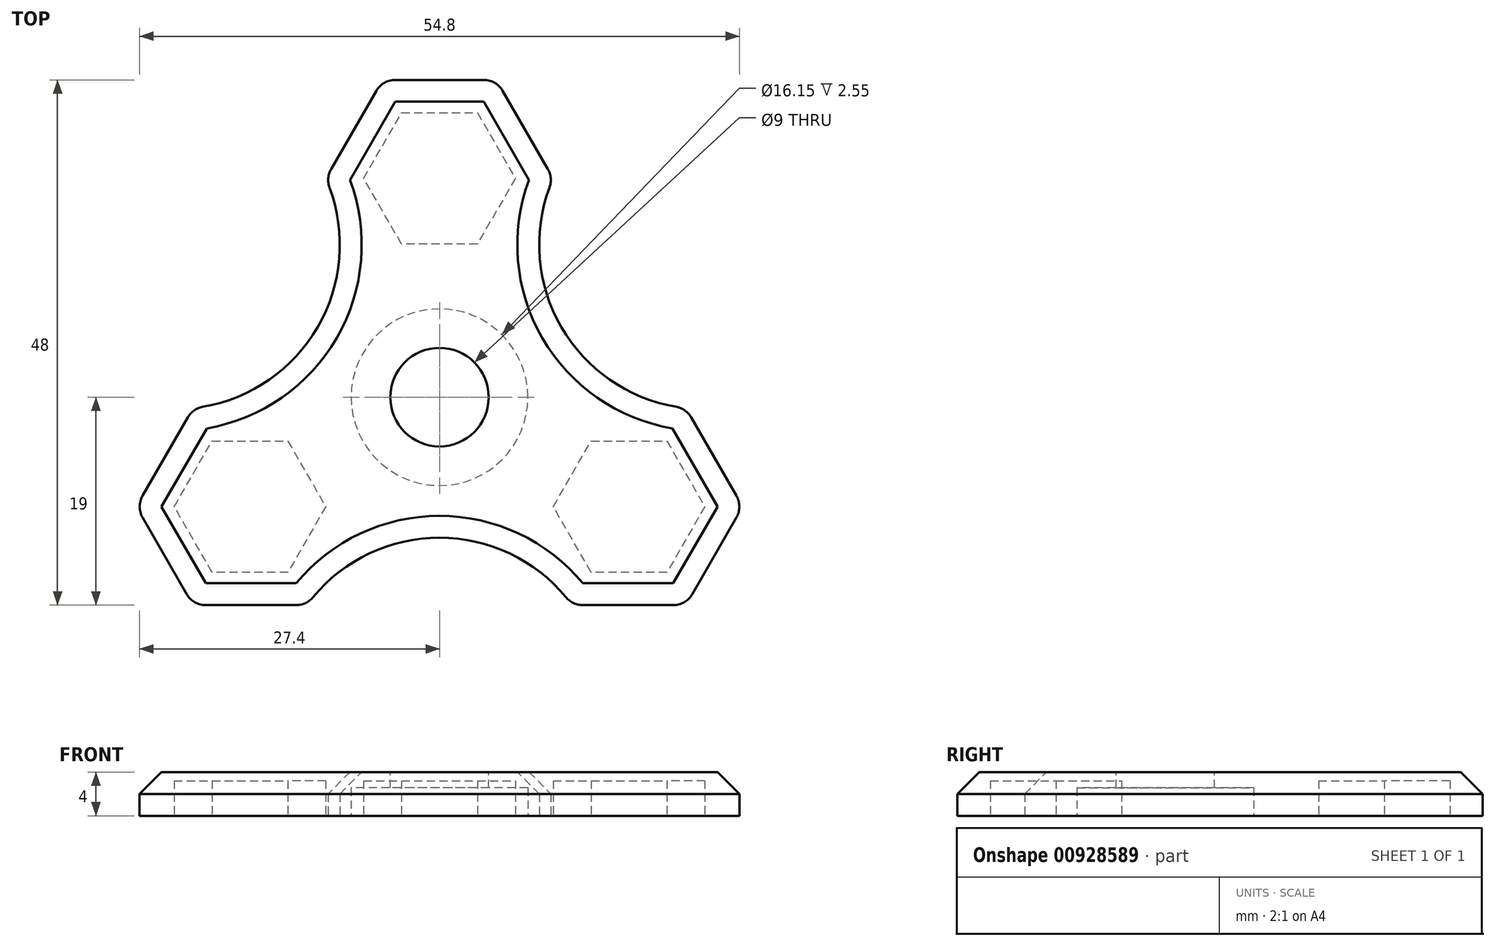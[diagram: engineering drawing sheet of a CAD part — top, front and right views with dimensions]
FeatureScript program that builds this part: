
annotation { "Feature Type Name" : "Feature", "Feature Type Description" : "" }
export const myFeature = defineFeature(function(context is Context, id is Id, definition is map)
    precondition{}
    {
        {
            var Q0;
            Q0=qCreatedBy(makeId("Top.planeOp"),FACE);
            var sketch = newSketch(context, id + "F0", { "sketchPlane" : qUnion([Q0])});
            skCircle(sketch, "E0", {"center": v(0, 0) * mm, "radius": 8 * mm, "construction": true});
            skCircle(sketch, "E1.cCircle", {"center": v(0, 20) * mm, "radius": 6 * mm, "construction": true});
            skLineSegment(sketch, "E1.0", {"start": v(3.46, 14) * mm, "end": v(-3.46, 14) * mm, "construction": true});
            skLineSegment(sketch, "E1.1", {"start": v(-3.46, 14) * mm, "end": v(-6.93, 20) * mm, "construction": true});
            skLineSegment(sketch, "E1.2", {"start": v(-6.93, 20) * mm, "end": v(-3.46, 26) * mm, "construction": true});
            skLineSegment(sketch, "E1.3", {"start": v(-3.46, 26) * mm, "end": v(3.46, 26) * mm, "construction": true});
            skLineSegment(sketch, "E1.4", {"start": v(3.46, 26) * mm, "end": v(6.93, 20) * mm, "construction": true});
            skLineSegment(sketch, "E1.5", {"start": v(6.93, 20) * mm, "end": v(3.46, 14) * mm, "construction": true});
            skPoint(sketch, "E1.0.midPoint", {"position": v(0, 14) * mm});
            skCircle(sketch, "E2.cCircle", {"center": v(0, 20) * mm, "radius": 9 * mm, "construction": true});
            skLineSegment(sketch, "E2.2", {"start": v(-9.9, 20.85) * mm, "end": v(-5.77, 28) * mm});
            skLineSegment(sketch, "E2.3", {"start": v(-4.04, 29) * mm, "end": v(4.04, 29) * mm});
            skLineSegment(sketch, "E2.4", {"start": v(5.77, 28) * mm, "end": v(9.9, 20.85) * mm});
            skPoint(sketch, "E2.0.midPoint", {"position": v(0, 11) * mm});
            skLineSegment(sketch, "E3.1.0", {"start": v(-23.1, -18) * mm, "end": v(-27.14, -11) * mm});
            skLineSegment(sketch, "E3.1.1", {"start": v(-27.14, -9) * mm, "end": v(-23, -1.85) * mm});
            skLineSegment(sketch, "E3.1.5", {"start": v(-13.1, -19) * mm, "end": v(-21.36, -19) * mm});
            skLineSegment(sketch, "E3.2.0", {"start": v(27.14, -11) * mm, "end": v(23.1, -18) * mm});
            skLineSegment(sketch, "E3.2.1", {"start": v(21.36, -19) * mm, "end": v(13.1, -19) * mm});
            skLineSegment(sketch, "E3.2.5", {"start": v(23, -1.85) * mm, "end": v(27.14, -9) * mm});
            skArc(sketch, "E4", {"start": v(10.05, 19.15) * mm, "mid": v(11.12, 6.42) * mm, "end": v(21.6, -0.87) * mm});
            skArc(sketch, "E5.1.0", {"start": v(-21.6, -0.87) * mm, "mid": v(-11.12, 6.42) * mm, "end": v(-10.05, 19.15) * mm});
            skArc(sketch, "E5.2.0", {"start": v(11.56, -18.28) * mm, "mid": v(0, -12.84) * mm, "end": v(-11.56, -18.28) * mm});
            skPoint(sketch, "E6.orphan", {"position": v(5.2, 11) * mm});
            skPoint(sketch, "E7.orphan", {"position": v(-5.2, 11) * mm});
            skPoint(sketch, "E8.visualSharp", {"position": v(-22.52, -1) * mm});
            skArc(sketch, "E8.filletArc", {"start": v(-21.6, -0.87) * mm, "mid": v(-22.42, -1.2) * mm, "end": v(-23, -1.85) * mm});
            skPoint(sketch, "E9.visualSharp", {"position": v(-27.71, -10) * mm});
            skArc(sketch, "E9.filletArc", {"start": v(-27.14, -9) * mm, "mid": v(-27.4, -10) * mm, "end": v(-27.14, -11) * mm});
            skPoint(sketch, "E10.visualSharp", {"position": v(-22.52, -19) * mm});
            skArc(sketch, "E10.filletArc", {"start": v(-23.1, -18) * mm, "mid": v(-22.36, -18.73) * mm, "end": v(-21.36, -19) * mm});
            skPoint(sketch, "E11.visualSharp", {"position": v(-12.12, -19) * mm});
            skArc(sketch, "E11.filletArc", {"start": v(-13.1, -19) * mm, "mid": v(-12.25, -18.81) * mm, "end": v(-11.56, -18.28) * mm});
            skPoint(sketch, "E12.visualSharp", {"position": v(12.12, -19) * mm});
            skArc(sketch, "E12.filletArc", {"start": v(11.56, -18.28) * mm, "mid": v(12.25, -18.81) * mm, "end": v(13.1, -19) * mm});
            skPoint(sketch, "E13.visualSharp", {"position": v(22.52, -19) * mm});
            skArc(sketch, "E13.filletArc", {"start": v(21.36, -19) * mm, "mid": v(22.36, -18.73) * mm, "end": v(23.1, -18) * mm});
            skPoint(sketch, "E14.visualSharp", {"position": v(27.71, -10) * mm});
            skArc(sketch, "E14.filletArc", {"start": v(27.14, -11) * mm, "mid": v(27.4, -10) * mm, "end": v(27.14, -9) * mm});
            skPoint(sketch, "E15.visualSharp", {"position": v(22.52, -1) * mm});
            skArc(sketch, "E15.filletArc", {"start": v(23, -1.85) * mm, "mid": v(22.42, -1.2) * mm, "end": v(21.6, -0.87) * mm});
            skPoint(sketch, "E16.visualSharp", {"position": v(10.4, 20) * mm});
            skArc(sketch, "E16.filletArc", {"start": v(10.05, 19.15) * mm, "mid": v(10.17, 20.01) * mm, "end": v(9.9, 20.85) * mm});
            skPoint(sketch, "E17.visualSharp", {"position": v(5.2, 29) * mm});
            skArc(sketch, "E17.filletArc", {"start": v(5.77, 28) * mm, "mid": v(5.04, 28.73) * mm, "end": v(4.04, 29) * mm});
            skPoint(sketch, "E18.visualSharp", {"position": v(-5.2, 29) * mm});
            skArc(sketch, "E18.filletArc", {"start": v(-4.04, 29) * mm, "mid": v(-5.04, 28.73) * mm, "end": v(-5.77, 28) * mm});
            skPoint(sketch, "E19.visualSharp", {"position": v(-10.4, 20) * mm});
            skArc(sketch, "E19.filletArc", {"start": v(-9.9, 20.85) * mm, "mid": v(-10.17, 20.01) * mm, "end": v(-10.05, 19.15) * mm});
            skSolve(sketch);
        }
        {
            var Q0;
            Q0 = qSketchRegion(id + "F0", true);
            extrude(context, id + "F1", {"entities" : qUnion([Q0]), "depth" : 4 * mm, "offsetDistance" : 25 * mm});
        }
        {
            var Q0;
            Q0=makeQuery(id+"F0.imprint","IMPRINT",FACE,{"disambiguationData":[TD([[makeQuery(id+"F0.imprint","IMPRINT",EDGE,{"derivedFrom":sQuery(id+"F0.wireOp",EDGE,"E2.2")}),-1.0]])]});
            var sketch = newSketch(context, id + "F2", { "sketchPlane" : qUnion([Q0])});
            skCircle(sketch, "E20", {"center": v(0, 0) * mm, "radius": 8.07 * mm});
            skSolve(sketch);
        }
        {
            var Q0;
            Q0 = qSketchRegion(id + "F2", true);
            extrude(context, id + "F3", {"entities" : qUnion([Q0]), "operationType" : NewBodyOperationType.REMOVE, "depth" : 2.55 * mm, "offsetDistance" : 25 * mm});
        }
        {
            var Q0;
            Q0=makeQuery(id+"F0.imprint","IMPRINT",FACE,{"disambiguationData":[TD([[makeQuery(id+"F0.imprint","IMPRINT",EDGE,{"derivedFrom":sQuery(id+"F0.wireOp",EDGE,"E2.2")}),-1.0]])]});
            var sketch = newSketch(context, id + "F4", { "sketchPlane" : qUnion([Q0])});
            skCircle(sketch, "E21.cCircle", {"center": v(0, 20) * mm, "radius": 6 * mm, "construction": true});
            skLineSegment(sketch, "E21.0", {"start": v(3.46, 26) * mm, "end": v(6.93, 20) * mm});
            skLineSegment(sketch, "E21.1", {"start": v(6.93, 20) * mm, "end": v(3.46, 14) * mm});
            skLineSegment(sketch, "E21.2", {"start": v(3.46, 14) * mm, "end": v(-3.46, 14) * mm});
            skLineSegment(sketch, "E21.3", {"start": v(-3.46, 14) * mm, "end": v(-6.93, 20) * mm});
            skLineSegment(sketch, "E21.4", {"start": v(-6.93, 20) * mm, "end": v(-3.46, 26) * mm});
            skLineSegment(sketch, "E21.5", {"start": v(-3.46, 26) * mm, "end": v(3.46, 26) * mm});
            skPoint(sketch, "E21.0.midPoint", {"position": v(5.2, 23) * mm});
            skLineSegment(sketch, "E22.1.0", {"start": v(-10.4, -10) * mm, "end": v(-13.86, -16) * mm});
            skLineSegment(sketch, "E22.1.1", {"start": v(-13.86, -4) * mm, "end": v(-10.4, -10) * mm});
            skLineSegment(sketch, "E22.1.2", {"start": v(-20.78, -4) * mm, "end": v(-13.86, -4) * mm});
            skLineSegment(sketch, "E22.1.3", {"start": v(-24.25, -10) * mm, "end": v(-20.78, -4) * mm});
            skLineSegment(sketch, "E22.1.4", {"start": v(-20.78, -16) * mm, "end": v(-24.25, -10) * mm});
            skLineSegment(sketch, "E22.1.5", {"start": v(-13.86, -16) * mm, "end": v(-20.78, -16) * mm});
            skLineSegment(sketch, "E22.2.0", {"start": v(13.86, -4) * mm, "end": v(20.78, -4) * mm});
            skLineSegment(sketch, "E22.2.1", {"start": v(10.4, -10) * mm, "end": v(13.86, -4) * mm});
            skLineSegment(sketch, "E22.2.2", {"start": v(13.86, -16) * mm, "end": v(10.4, -10) * mm});
            skLineSegment(sketch, "E22.2.3", {"start": v(20.78, -16) * mm, "end": v(13.86, -16) * mm});
            skLineSegment(sketch, "E22.2.4", {"start": v(24.25, -10) * mm, "end": v(20.78, -16) * mm});
            skLineSegment(sketch, "E22.2.5", {"start": v(20.78, -4) * mm, "end": v(24.25, -10) * mm});
            skPoint(sketch, "E22.center", {"position": v(0, 0) * mm});
            skSolve(sketch);
        }
        {
            var Q0;
            Q0 = qSketchRegion(id + "F4", true);
            extrude(context, id + "F5", {"entities" : qUnion([Q0]), "operationType" : NewBodyOperationType.REMOVE, "depth" : 3.2 * mm, "offsetDistance" : 25 * mm});
        }
        {
            var Q0;
            Q0=makeQuery(id+"F1.opExtrude","CAP_FACE",FACE,{"disambiguationData":[OSD([sQuery(id+"F0.wireOp",EDGE,"E2.2"),sQuery(id+"F0.wireOp",EDGE,"E2.3"),sQuery(id+"F0.wireOp",EDGE,"E2.4"),sQuery(id+"F0.wireOp",EDGE,"E3.1.0"),sQuery(id+"F0.wireOp",EDGE,"E3.1.1"),sQuery(id+"F0.wireOp",EDGE,"E3.1.5"),sQuery(id+"F0.wireOp",EDGE,"E3.2.0"),sQuery(id+"F0.wireOp",EDGE,"E3.2.1"),sQuery(id+"F0.wireOp",EDGE,"E3.2.5"),sQuery(id+"F0.wireOp",EDGE,"E4"),sQuery(id+"F0.wireOp",EDGE,"E5.1.0"),sQuery(id+"F0.wireOp",EDGE,"E5.2.0"),sQuery(id+"F0.wireOp",EDGE,"E8.filletArc"),sQuery(id+"F0.wireOp",EDGE,"E9.filletArc"),sQuery(id+"F0.wireOp",EDGE,"E10.filletArc"),sQuery(id+"F0.wireOp",EDGE,"E11.filletArc"),sQuery(id+"F0.wireOp",EDGE,"E12.filletArc"),sQuery(id+"F0.wireOp",EDGE,"E13.filletArc"),sQuery(id+"F0.wireOp",EDGE,"E14.filletArc"),sQuery(id+"F0.wireOp",EDGE,"E15.filletArc"),sQuery(id+"F0.wireOp",EDGE,"E16.filletArc"),sQuery(id+"F0.wireOp",EDGE,"E17.filletArc"),sQuery(id+"F0.wireOp",EDGE,"E18.filletArc"),sQuery(id+"F0.wireOp",EDGE,"E19.filletArc")])],"isStart":false});
            chamfer(context, id + "F6", {"entities" : qUnion([Q0]), "width" : 2 * mm, "tangentPropagation" : true});
        }
        {
            var Q0;
            Q0=makeQuery(id+"F1.opExtrude","CAP_FACE",FACE,{"disambiguationData":[OSD([sQuery(id+"F0.wireOp",EDGE,"E2.2"),sQuery(id+"F0.wireOp",EDGE,"E2.3"),sQuery(id+"F0.wireOp",EDGE,"E2.4"),sQuery(id+"F0.wireOp",EDGE,"E3.1.0"),sQuery(id+"F0.wireOp",EDGE,"E3.1.1"),sQuery(id+"F0.wireOp",EDGE,"E3.1.5"),sQuery(id+"F0.wireOp",EDGE,"E3.2.0"),sQuery(id+"F0.wireOp",EDGE,"E3.2.1"),sQuery(id+"F0.wireOp",EDGE,"E3.2.5"),sQuery(id+"F0.wireOp",EDGE,"E4"),sQuery(id+"F0.wireOp",EDGE,"E5.1.0"),sQuery(id+"F0.wireOp",EDGE,"E5.2.0"),sQuery(id+"F0.wireOp",EDGE,"E8.filletArc"),sQuery(id+"F0.wireOp",EDGE,"E9.filletArc"),sQuery(id+"F0.wireOp",EDGE,"E10.filletArc"),sQuery(id+"F0.wireOp",EDGE,"E11.filletArc"),sQuery(id+"F0.wireOp",EDGE,"E12.filletArc"),sQuery(id+"F0.wireOp",EDGE,"E13.filletArc"),sQuery(id+"F0.wireOp",EDGE,"E14.filletArc"),sQuery(id+"F0.wireOp",EDGE,"E15.filletArc"),sQuery(id+"F0.wireOp",EDGE,"E16.filletArc"),sQuery(id+"F0.wireOp",EDGE,"E17.filletArc"),sQuery(id+"F0.wireOp",EDGE,"E18.filletArc"),sQuery(id+"F0.wireOp",EDGE,"E19.filletArc")])],"isStart":false});
            var sketch = newSketch(context, id + "F7", { "sketchPlane" : qUnion([Q0])});
            skCircle(sketch, "E23", {"center": v(0, 0) * mm, "radius": 4.5 * mm});
            skSolve(sketch);
        }
        {
            var Q0;
            Q0 = qSketchRegion(id + "F7", true);
            extrude(context, id + "F8", {"entities" : qUnion([Q0]), "operationType" : NewBodyOperationType.REMOVE, "oppositeDirection" : true, "depth" : 25 * mm, "offsetDistance" : 25 * mm});
        }
    });
